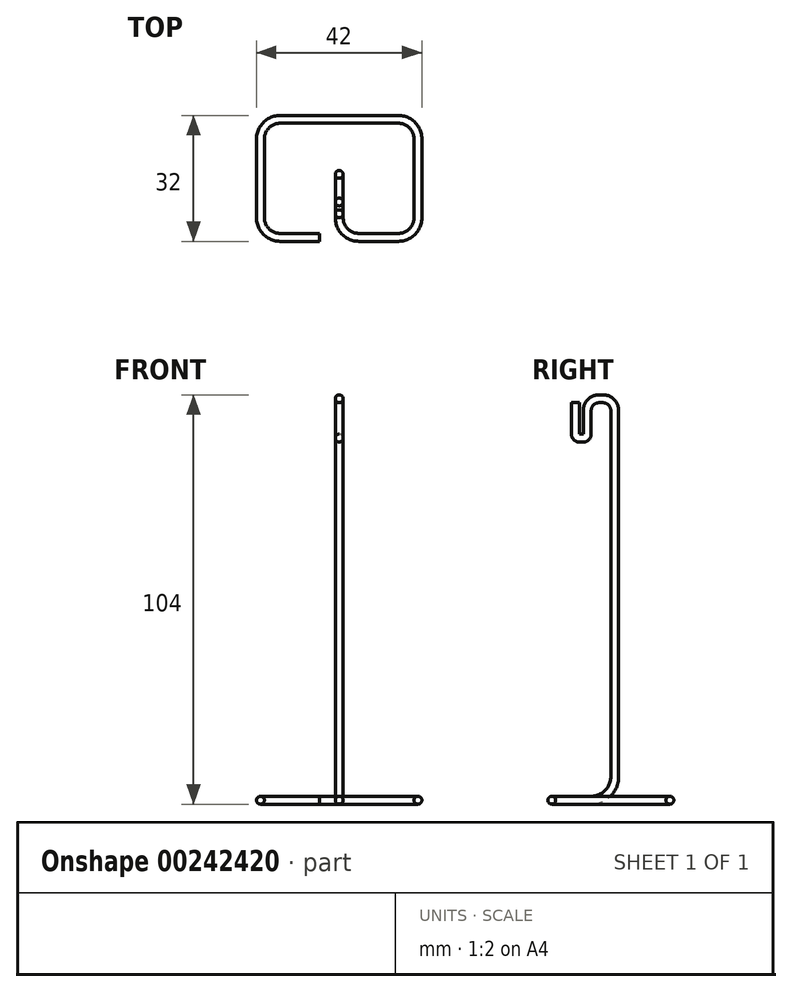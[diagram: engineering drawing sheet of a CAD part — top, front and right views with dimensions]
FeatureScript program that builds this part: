
annotation { "Feature Type Name" : "Feature", "Feature Type Description" : "" }
export const myFeature = defineFeature(function(context is Context, id is Id, definition is map)
    precondition{}
    {
        {
            var Q0;
            Q0=qCreatedBy(makeId("Right.planeOp"),FACE);
            var sketch = newSketch(context, id + "F0", { "sketchPlane" : qUnion([Q0])});
            skLineSegment(sketch, "E0", {"start": v(0, 100) * mm, "end": v(0, 92) * mm});
            skLineSegment(sketch, "E1", {"start": v(2, 90) * mm, "end": v(3, 90) * mm});
            skLineSegment(sketch, "E2", {"start": v(5, 92) * mm, "end": v(5, 98) * mm});
            skLineSegment(sketch, "E3", {"start": v(7, 100) * mm, "end": v(8, 100) * mm});
            skLineSegment(sketch, "E4", {"start": v(10, 98) * mm, "end": v(10, 5) * mm});
            skLineSegment(sketch, "E5", {"start": v(5, 0) * mm, "end": v(0, 0) * mm});
            skPoint(sketch, "E6.visualSharp", {"position": v(0, 90) * mm});
            skArc(sketch, "E6.filletArc", {"start": v(0, 92) * mm, "mid": v(0.59, 90.59) * mm, "end": v(2, 90) * mm});
            skPoint(sketch, "E7.visualSharp", {"position": v(5, 90) * mm});
            skArc(sketch, "E7.filletArc", {"start": v(3, 90) * mm, "mid": v(4.41, 90.59) * mm, "end": v(5, 92) * mm});
            skPoint(sketch, "E8.visualSharp", {"position": v(5, 100) * mm});
            skArc(sketch, "E8.filletArc", {"start": v(7, 100) * mm, "mid": v(5.59, 99.41) * mm, "end": v(5, 98) * mm});
            skPoint(sketch, "E9.visualSharp", {"position": v(10, 100) * mm});
            skArc(sketch, "E9.filletArc", {"start": v(10, 98) * mm, "mid": v(9.41, 99.41) * mm, "end": v(8, 100) * mm});
            skPoint(sketch, "E10.visualSharp", {"position": v(10, 0) * mm});
            skArc(sketch, "E10.filletArc", {"start": v(5, 0) * mm, "mid": v(8.54, 1.46) * mm, "end": v(10, 5) * mm});
            skSolve(sketch);
        }
        {
            var Q0;
            Q0=sQuery(id+"F0.wireOp",VERTEX,"E0.start");
            var Q1;
            Q1=qCreatedBy(makeId("Top.planeOp"),FACE);
            cPlane(context, id + "F1", {"entities" : qUnion([Q0, Q1]), "cplaneType" : CPlaneType.PLANE_POINT, "offset" : 25 * mm, "width" : 150 * mm, "height" : 150 * mm});
        }
        {
            var Q0;
            Q0=qCreatedBy(id+"F1.planeOp",FACE);
            var sketch = newSketch(context, id + "F2", { "sketchPlane" : qUnion([Q0])});
            skCircle(sketch, "E11", {"center": v(0, 1) * mm, "radius": 1 * mm});
            skSolve(sketch);
        }
        {
            var Q0;
            Q0=makeQuery(id+"F2.imprint","IMPRINT",FACE,{"disambiguationData":[TD([[makeQuery(id+"F2.imprint","IMPRINT",EDGE,{"derivedFrom":sQuery(id+"F2.wireOp",EDGE,"E11")}),1.0]])]});
            var Q1;
            Q1=sQuery(id+"F0.wireOp",EDGE,"E0");
            var Q2;
            Q2=sQuery(id+"F0.wireOp",EDGE,"E6.filletArc");
            var Q3;
            Q3=sQuery(id+"F0.wireOp",EDGE,"E1");
            var Q4;
            Q4=sQuery(id+"F0.wireOp",EDGE,"E7.filletArc");
            var Q5;
            Q5=sQuery(id+"F0.wireOp",EDGE,"E2");
            var Q6;
            Q6=sQuery(id+"F0.wireOp",EDGE,"E9.filletArc");
            var Q7;
            Q7=sQuery(id+"F0.wireOp",EDGE,"E3");
            var Q8;
            Q8=sQuery(id+"F0.wireOp",EDGE,"E8.filletArc");
            var Q9;
            Q9=sQuery(id+"F0.wireOp",EDGE,"E4");
            var Q10;
            Q10=sQuery(id+"F0.wireOp",EDGE,"E10.filletArc");
            var Q11;
            Q11=sQuery(id+"F0.wireOp",EDGE,"E5");
            sweep(context, id + "F3", {"profiles" : qUnion([Q0]), "path" : qUnion([Q1, Q2, Q3, Q4, Q5, Q6, Q7, Q8, Q9, Q10, Q11])});
        }
        {
            var Q0;
            Q0=qCreatedBy(makeId("Top.planeOp"),FACE);
            var sketch = newSketch(context, id + "F4", { "sketchPlane" : qUnion([Q0])});
            skLineSegment(sketch, "E12", {"start": v(0, 0) * mm, "end": v(0, 0) * mm});
            skLineSegment(sketch, "E13", {"start": v(5, -5) * mm, "end": v(15, -5) * mm});
            skLineSegment(sketch, "E14", {"start": v(20, 0) * mm, "end": v(20, 20) * mm});
            skLineSegment(sketch, "E15", {"start": v(15, 25) * mm, "end": v(-15, 25) * mm});
            skLineSegment(sketch, "E16", {"start": v(-20, 20) * mm, "end": v(-20, 0) * mm});
            skLineSegment(sketch, "E17", {"start": v(-15, -5) * mm, "end": v(-5, -5) * mm});
            skPoint(sketch, "E18.visualSharp", {"position": v(-20, -5) * mm});
            skArc(sketch, "E18.filletArc", {"start": v(-20, 0) * mm, "mid": v(-18.54, -3.54) * mm, "end": v(-15, -5) * mm});
            skPoint(sketch, "E19.visualSharp", {"position": v(20, -5) * mm});
            skArc(sketch, "E19.filletArc", {"start": v(15, -5) * mm, "mid": v(18.54, -3.54) * mm, "end": v(20, 0) * mm});
            skPoint(sketch, "E20.visualSharp", {"position": v(20, 25) * mm});
            skArc(sketch, "E20.filletArc", {"start": v(20, 20) * mm, "mid": v(18.54, 23.54) * mm, "end": v(15, 25) * mm});
            skPoint(sketch, "E21.visualSharp", {"position": v(-20, 25) * mm});
            skArc(sketch, "E21.filletArc", {"start": v(-15, 25) * mm, "mid": v(-18.54, 23.54) * mm, "end": v(-20, 20) * mm});
            skPoint(sketch, "E22.visualSharp", {"position": v(0, -5) * mm});
            skArc(sketch, "E22.filletArc", {"start": v(0, 0) * mm, "mid": v(1.46, -3.54) * mm, "end": v(5, -5) * mm});
            skSolve(sketch);
        }
        {
            var Q0;
            Q0=makeQuery(id+"F3.opSweep","CAP_FACE",FACE,{"disambiguationData":[OSD([sQuery(id+"F0.wireOp",VERTEX,"E5.end"),sQuery(id+"F2.wireOp",EDGE,"E11")])],"isStart":false});
            var Q1;
            Q1=sQuery(id+"F4.wireOp",EDGE,"E22.filletArc");
            var Q2;
            Q2=sQuery(id+"F4.wireOp",EDGE,"E13");
            var Q3;
            Q3=sQuery(id+"F4.wireOp",EDGE,"E19.filletArc");
            var Q4;
            Q4=sQuery(id+"F4.wireOp",EDGE,"E14");
            var Q5;
            Q5=sQuery(id+"F4.wireOp",EDGE,"E20.filletArc");
            var Q6;
            Q6=sQuery(id+"F4.wireOp",EDGE,"E15");
            var Q7;
            Q7=sQuery(id+"F4.wireOp",EDGE,"E21.filletArc");
            var Q8;
            Q8=sQuery(id+"F4.wireOp",EDGE,"E16");
            var Q9;
            Q9=sQuery(id+"F4.wireOp",EDGE,"E18.filletArc");
            var Q10;
            Q10=sQuery(id+"F4.wireOp",EDGE,"E17");
            sweep(context, id + "F5", {"operationType" : NewBodyOperationType.ADD, "profiles" : qUnion([Q0]), "path" : qUnion([Q1, Q2, Q3, Q4, Q5, Q6, Q7, Q8, Q9, Q10])});
        }
    });
